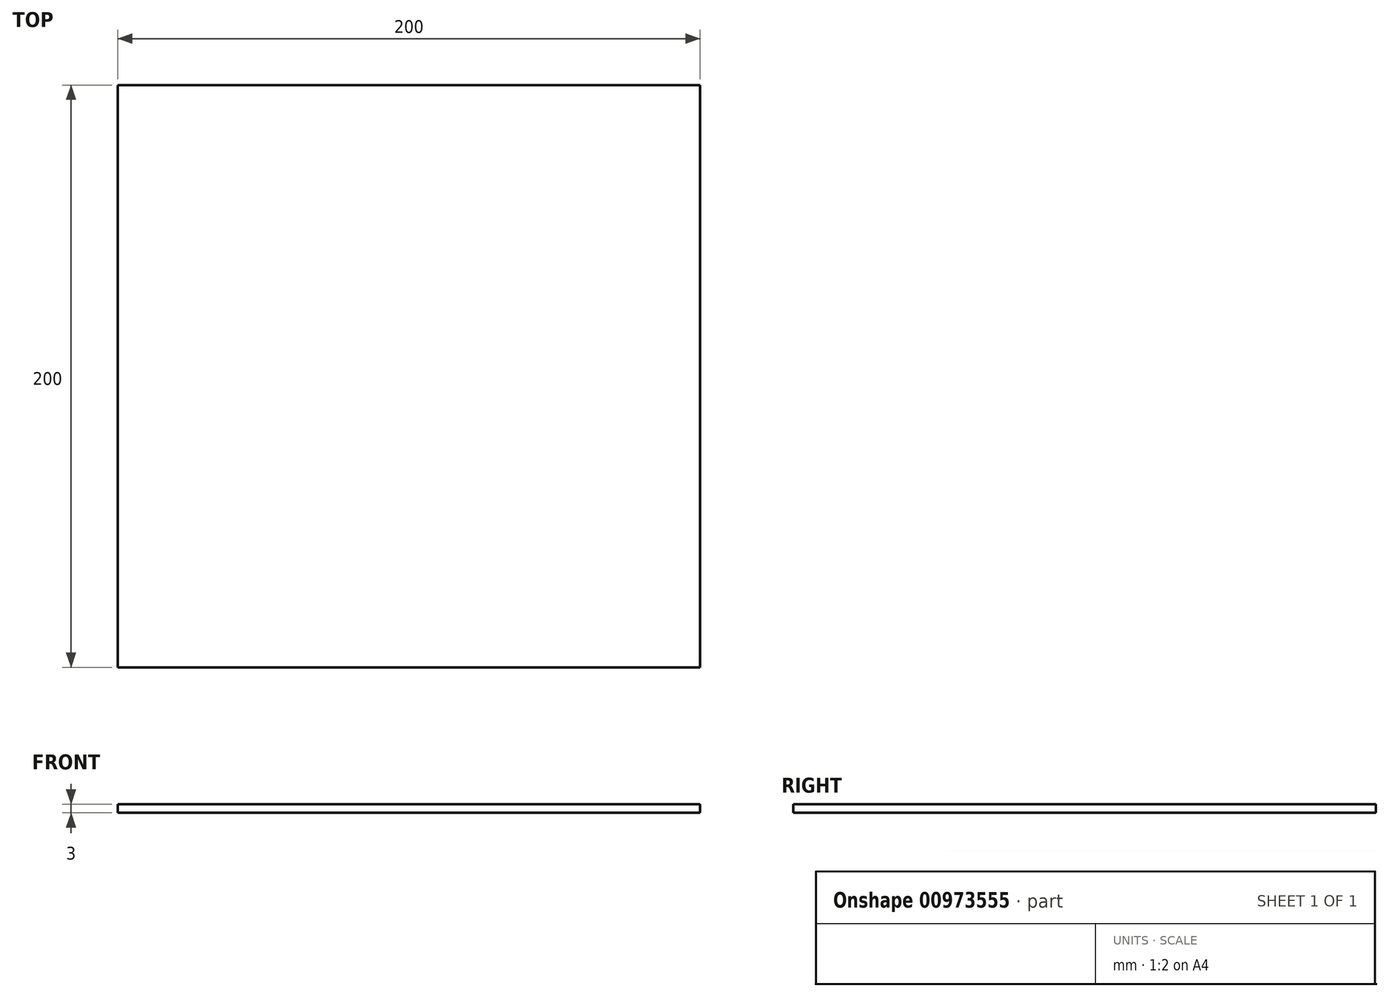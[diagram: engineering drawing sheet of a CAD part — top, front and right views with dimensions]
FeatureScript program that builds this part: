
annotation { "Feature Type Name" : "Feature", "Feature Type Description" : "" }
export const myFeature = defineFeature(function(context is Context, id is Id, definition is map)
    precondition{}
    {
        {
            var Q0;
            Q0=qCreatedBy(makeId("Top.planeOp"),FACE);
            var sketch = newSketch(context, id + "F0", { "sketchPlane" : qUnion([Q0])});
            skLineSegment(sketch, "E0.bottom", {"start": v(100, -100) * mm, "end": v(-100, -100) * mm});
            skLineSegment(sketch, "E0.top", {"start": v(100, 100) * mm, "end": v(-100, 100) * mm});
            skLineSegment(sketch, "E0.left", {"start": v(100, -100) * mm, "end": v(100, 100) * mm});
            skLineSegment(sketch, "E0.right", {"start": v(-100, -100) * mm, "end": v(-100, 100) * mm});
            skPoint(sketch, "E0.middle", {"position": v(0, 0) * mm});
            skSolve(sketch);
        }
        {
            var Q0;
            Q0 = qSketchRegion(id + "F0", true);
            extrude(context, id + "F1", {"entities" : qUnion([Q0]), "depth" : 3 * mm, "offsetDistance" : 25 * mm});
        }
    });
